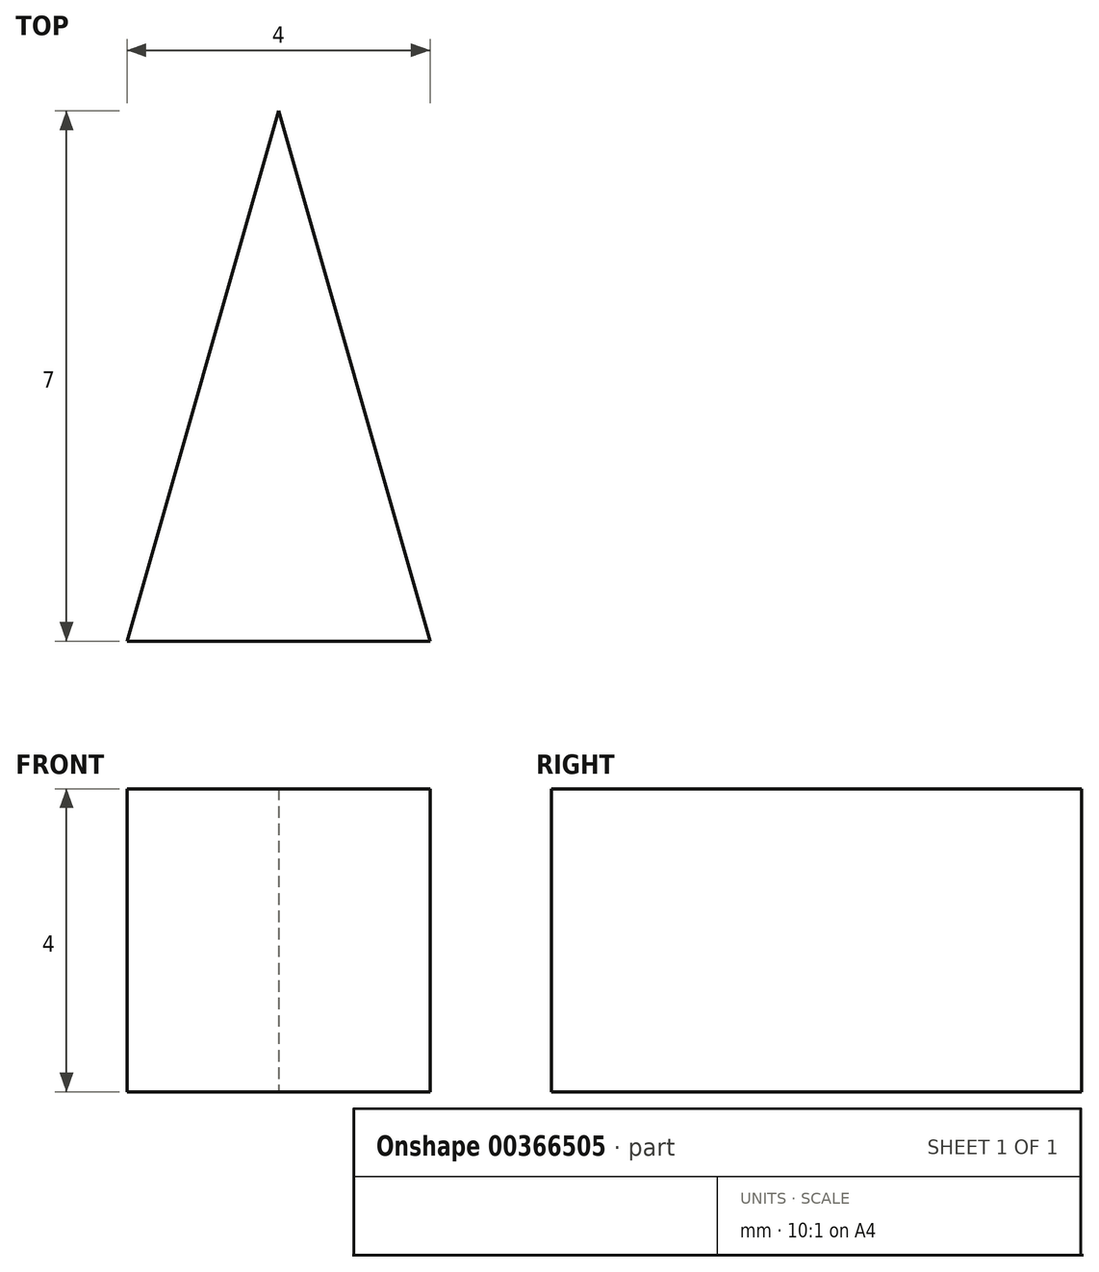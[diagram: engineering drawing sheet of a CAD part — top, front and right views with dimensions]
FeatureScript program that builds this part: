
annotation { "Feature Type Name" : "Feature", "Feature Type Description" : "" }
export const myFeature = defineFeature(function(context is Context, id is Id, definition is map)
    precondition{}
    {
        {
            var Q0;
            Q0=qCreatedBy(makeId("Top.planeOp"),FACE);
            var sketch = newSketch(context, id + "F0", { "sketchPlane" : qUnion([Q0])});
            skLineSegment(sketch, "E0", {"start": v(0, 0) * mm, "end": v(4, 0) * mm});
            skLineSegment(sketch, "E1", {"start": v(4, 0) * mm, "end": v(4, 7) * mm});
            skLineSegment(sketch, "E2", {"start": v(4, 7) * mm, "end": v(0, 7) * mm});
            skLineSegment(sketch, "E3", {"start": v(0, 7) * mm, "end": v(0, 0) * mm});
            skSolve(sketch);
        }
        {
            var Q0;
            Q0=qSketchRegion(id+"F0",true);
            extrude(context, id + "F1", {"entities" : qUnion([Q0]), "depth" : 4 * mm});
        }
        {
            var Q0;
            Q0=makeQuery(id+"F1.opExtrude","SWEPT_FACE",FACE,{"disambiguationData":[OSD([sQuery(id+"F0.wireOp",EDGE,"E2")])]});
            var sketch = newSketch(context, id + "F2", { "sketchPlane" : qUnion([Q0])});
            skLineSegment(sketch, "E4", {"start": v(0, 0) * mm, "end": v(-4, 4) * mm});
            skLineSegment(sketch, "E5", {"start": v(-4, 0) * mm, "end": v(0, 4) * mm});
            skSolve(sketch);
        }
        {
            var Q0;
            Q0=sQuery(id+"F2.wireOp",EDGE,"E5");
            cPoint(context, id + "F3", {"entities" : qUnion([Q0]), "parameter" : 0.5});
        }
        {
            var Q0;
            Q0=qCreatedBy(id+"F3",VERTEX);
            var Q1;
            Q1=makeQuery(id+"F1.opExtrude","CAP_VERTEX",VERTEX,{"disambiguationData":[OSD([sQuery(id+"F0.wireOp",EDGE,"E0"),sQuery(id+"F0.wireOp",EDGE,"E1")])],"isStart":false});
            var Q2;
            Q2=makeQuery(id+"F1.opExtrude","CAP_VERTEX",VERTEX,{"disambiguationData":[OSD([sQuery(id+"F0.wireOp",EDGE,"E0"),sQuery(id+"F0.wireOp",EDGE,"E1")])],"isStart":true});
            cPlane(context, id + "F4", {"entities" : qUnion([Q0, Q1, Q2]), "cplaneType" : CPlaneType.THREE_POINT, "offset" : 25 * mm, "width" : 150 * mm, "height" : 150 * mm});
        }
        {
            var Q0;
            Q0=qCreatedBy(id+"F4.planeOp",FACE);
            var sketch = newSketch(context, id + "F5", { "sketchPlane" : qUnion([Q0])});
            skLineSegment(sketch, "E6", {"start": v(7.06, 9.72) * mm, "end": v(-14.32, 4.8) * mm});
            skLineSegment(sketch, "E7", {"start": v(-14.32, 4.8) * mm, "end": v(-11.36, -8.08) * mm});
            skLineSegment(sketch, "E8", {"start": v(-11.36, -8.08) * mm, "end": v(9.26, -3.33) * mm});
            skLineSegment(sketch, "E9", {"start": v(9.26, -3.33) * mm, "end": v(7.06, 9.72) * mm});
            skSolve(sketch);
        }
        {
            var Q0;
            Q0=qSketchRegion(id+"F5",true);
            extrude(context, id + "F6", {"entities" : qUnion([Q0]), "operationType" : NewBodyOperationType.REMOVE, "oppositeDirection" : true, "depth" : 25 * mm});
        }
        {
            var Q0;
            Q0=sQuery(id+"F2.wireOp",EDGE,"E5");
            cPoint(context, id + "F7", {"entities" : qUnion([Q0]), "parameter" : 0.5});
        }
        {
            var Q0;
            Q0=qCreatedBy(id+"F7",VERTEX);
            var Q1;
            Q1=makeQuery(id+"F1.opExtrude","CAP_VERTEX",VERTEX,{"disambiguationData":[OSD([sQuery(id+"F0.wireOp",EDGE,"E0"),sQuery(id+"F0.wireOp",EDGE,"E3")])],"isStart":false});
            var Q2;
            Q2=qCreatedBy(makeId("Origin.pointOp"),VERTEX);
            cPlane(context, id + "F8", {"entities" : qUnion([Q0, Q1, Q2]), "cplaneType" : CPlaneType.THREE_POINT, "offset" : 25 * mm, "width" : 150 * mm, "height" : 150 * mm});
        }
        {
            var Q0;
            Q0=qCreatedBy(id+"F8.planeOp",FACE);
            var sketch = newSketch(context, id + "F9", { "sketchPlane" : qUnion([Q0])});
            skLineSegment(sketch, "E10", {"start": v(-6.77, -9.41) * mm, "end": v(6.3, -9.41) * mm});
            skLineSegment(sketch, "E11", {"start": v(6.3, -9.41) * mm, "end": v(3.88, 17.09) * mm});
            skLineSegment(sketch, "E12", {"start": v(3.88, 17.09) * mm, "end": v(-6.92, 14.66) * mm});
            skLineSegment(sketch, "E13", {"start": v(-6.92, 14.66) * mm, "end": v(-10.43, 17.94) * mm});
            skLineSegment(sketch, "E14", {"start": v(-10.43, 17.94) * mm, "end": v(-10.43, -10) * mm});
            skLineSegment(sketch, "E15", {"start": v(-10.43, -10) * mm, "end": v(-6.77, -9.41) * mm});
            skSolve(sketch);
        }
        {
            var Q0;
            Q0=qSketchRegion(id+"F9",true);
            extrude(context, id + "F10", {"entities" : qUnion([Q0]), "operationType" : NewBodyOperationType.REMOVE, "depth" : 25 * mm});
        }
    });
